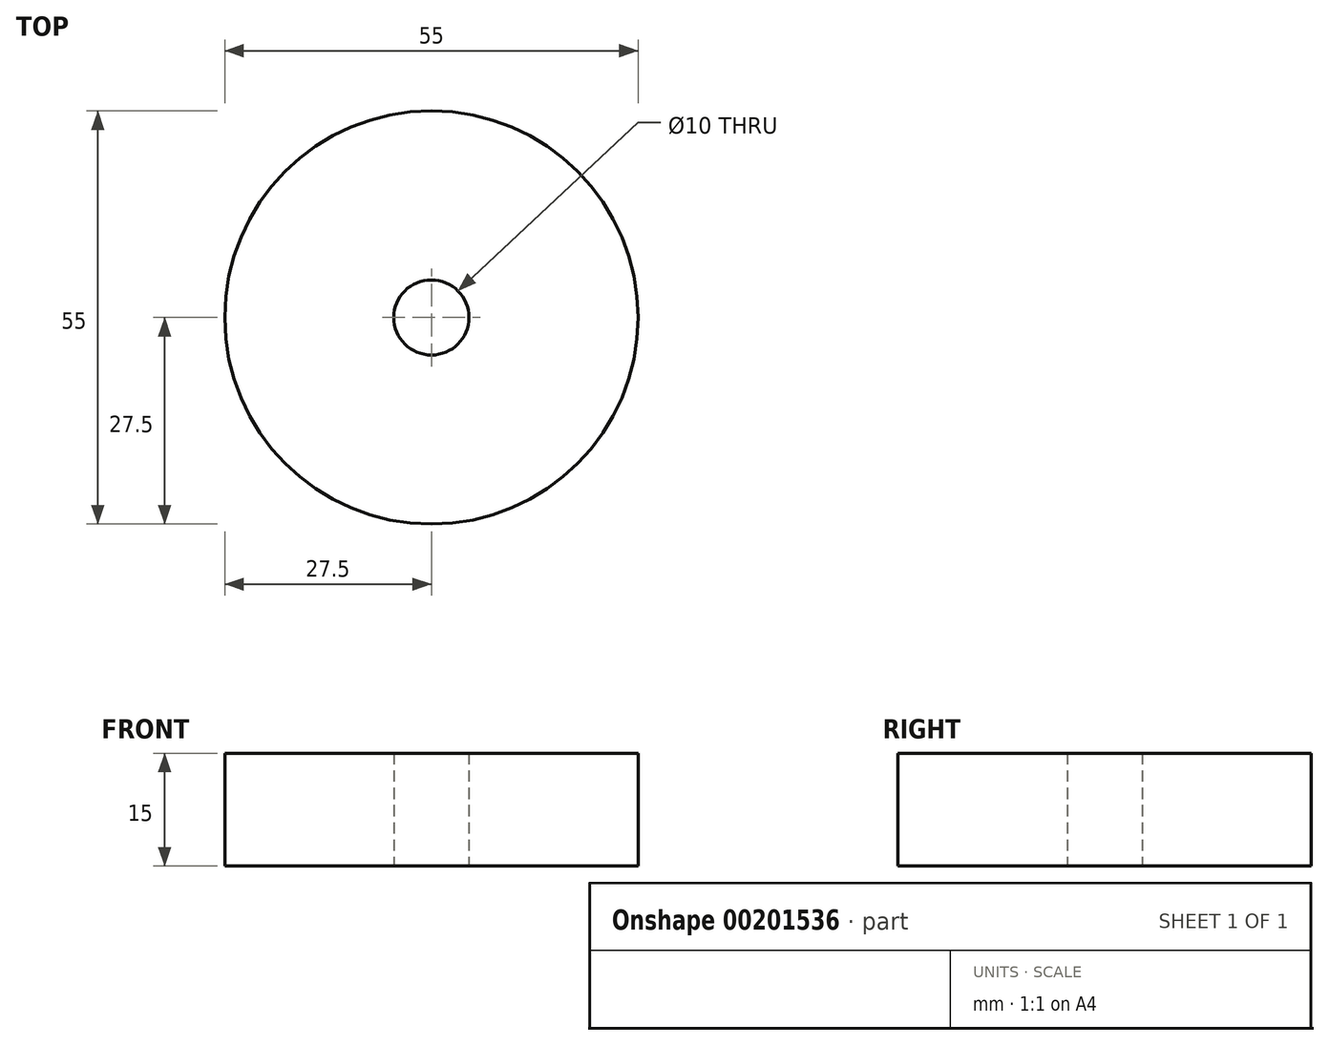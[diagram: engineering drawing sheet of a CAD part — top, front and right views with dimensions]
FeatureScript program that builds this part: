
annotation { "Feature Type Name" : "Feature", "Feature Type Description" : "" }
export const myFeature = defineFeature(function(context is Context, id is Id, definition is map)
    precondition{}
    {
        {
            var Q0;
            Q0=qCreatedBy(makeId("Top.planeOp"),FACE);
            var sketch = newSketch(context, id + "F0", { "sketchPlane" : qUnion([Q0])});
            skCircle(sketch, "E0", {"center": v(0, 0) * mm, "radius": 27.5 * mm});
            skCircle(sketch, "E1", {"center": v(0, 0) * mm, "radius": 5 * mm});
            skSolve(sketch);
        }
        {
            var Q0;
            Q0 = qSketchRegion(id + "F0", true);
            extrude(context, id + "F1", {"entities" : qUnion([Q0]), "depth" : 15 * mm});
        }
    });
